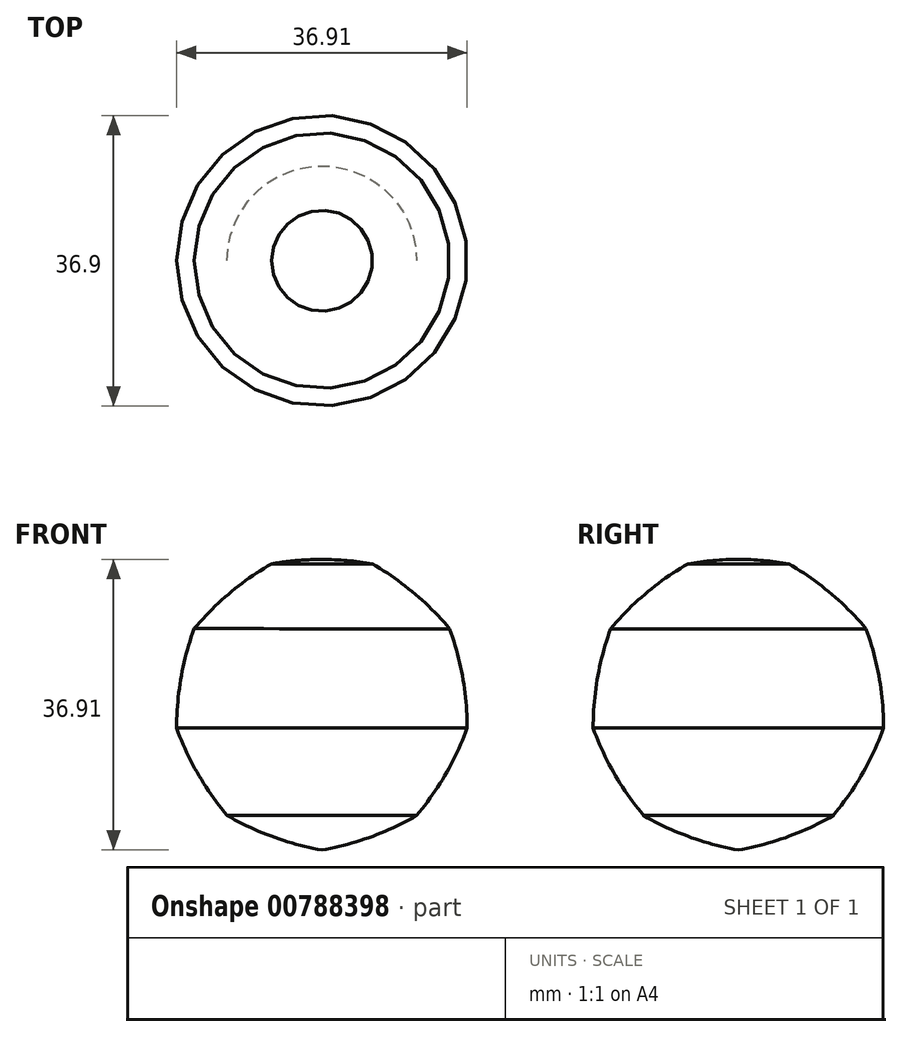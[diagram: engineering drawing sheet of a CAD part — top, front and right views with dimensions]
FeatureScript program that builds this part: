
annotation { "Feature Type Name" : "Feature", "Feature Type Description" : "" }
export const myFeature = defineFeature(function(context is Context, id is Id, definition is map)
    precondition{}
    {
        {
            var Q0;
            Q0=qCreatedBy(makeId("Front.planeOp"),FACE);
            var sketch = newSketch(context, id + "F0", { "sketchPlane" : qUnion([Q0])});
            skArc(sketch, "E0", {"start": v(-16.23, 9.38) * mm, "mid": v(-17.9, 3.16) * mm, "end": v(-18.46, -3.25) * mm});
            skArc(sketch, "E1.trimOffspring", {"start": v(6.42, 17.6) * mm, "mid": v(0, 18.17) * mm, "end": v(-6.4, 17.61) * mm});
            skArc(sketch, "E2.trimOffspring", {"start": v(16.23, 9.36) * mm, "mid": v(11.69, 13.91) * mm, "end": v(6.42, 17.6) * mm});
            skArc(sketch, "E3.trimOffspring", {"start": v(18.45, -3.26) * mm, "mid": v(17.9, 3.15) * mm, "end": v(16.23, 9.36) * mm});
            skArc(sketch, "E4.trimOffspring", {"start": v(12.04, -14.36) * mm, "mid": v(15.73, -9.1) * mm, "end": v(18.45, -3.26) * mm});
            skArc(sketch, "E5.trimOffspring", {"start": v(0, -18.74) * mm, "mid": v(6.2, -17.08) * mm, "end": v(12.04, -14.36) * mm});
            skArc(sketch, "E6.trimOffspring", {"start": v(-12.05, -14.35) * mm, "mid": v(-6.22, -17.07) * mm, "end": v(0, -18.74) * mm});
            skArc(sketch, "E7.trimOffspring", {"start": v(-18.46, -3.25) * mm, "mid": v(-15.74, -9.08) * mm, "end": v(-12.05, -14.35) * mm});
            skArc(sketch, "E8.trimOffspring", {"start": v(-6.4, 17.61) * mm, "mid": v(-11.67, 13.93) * mm, "end": v(-16.23, 9.38) * mm});
            skLineSegment(sketch, "E9", {"start": v(0, -18.74) * mm, "end": v(0, 18.17) * mm});
            skSolve(sketch);
        }
        {
            var Q0;
            Q0=makeQuery(id+"F0.imprint","IMPRINT",FACE,{"disambiguationData":[TD([[makeQuery(id+"F0.imprint","IMPRINT",EDGE,{"derivedFrom":sQuery(id+"F0.wireOp",EDGE,"E0")}),1.0]])]});
            var Q1;
            Q1=sQuery(id+"F0.wireOp",EDGE,"E9");
            revolve(context, id + "F1", {"surfaceOperationType" : NewSurfaceOperationType.NEW, "entities" : qUnion([Q0]), "axis" : qUnion([Q1]), "revolveType" : RevolveType.FULL});
        }
    });
